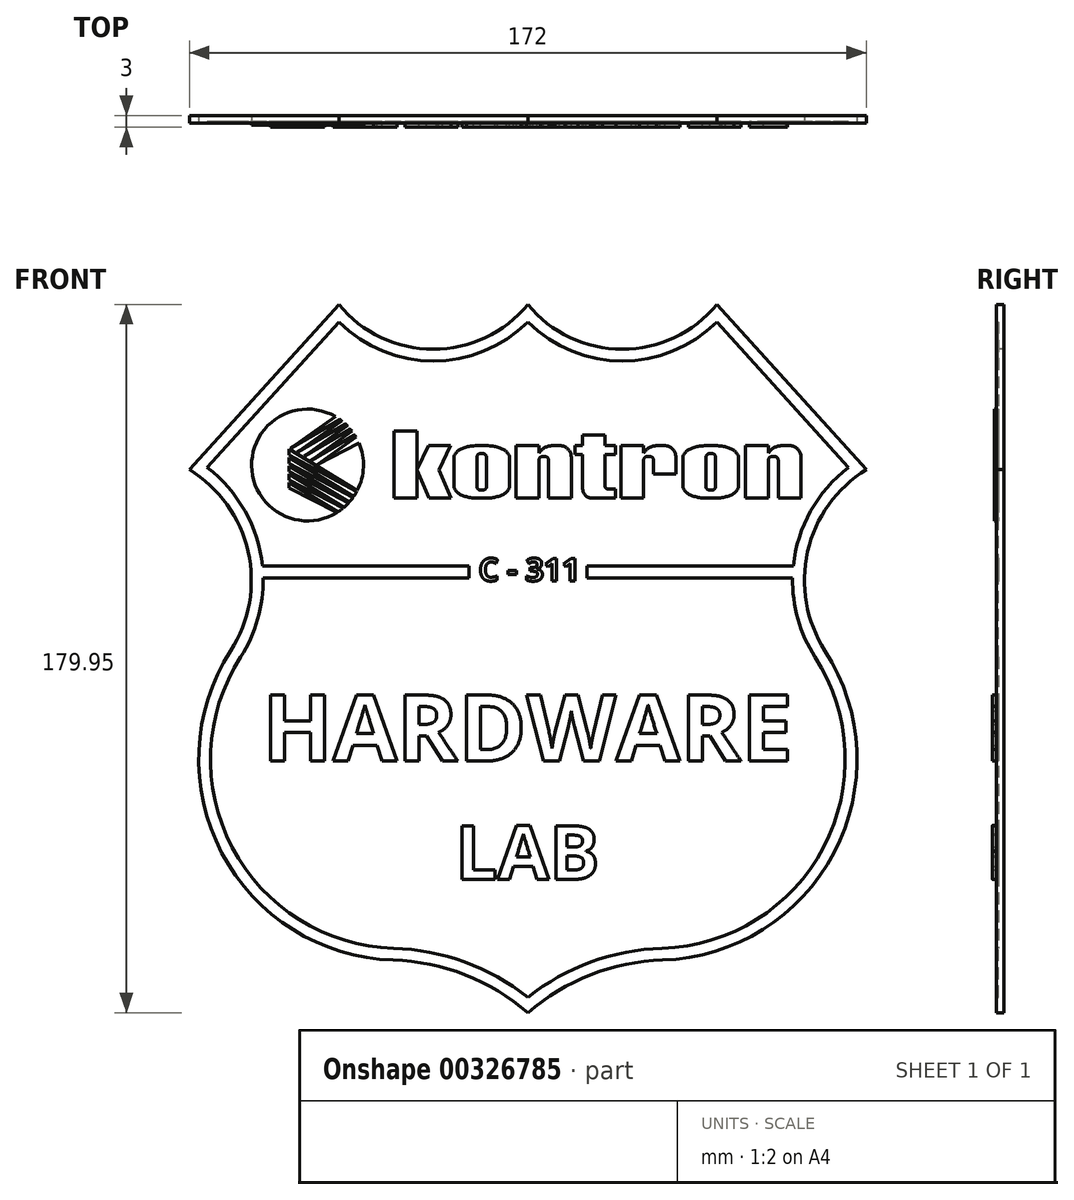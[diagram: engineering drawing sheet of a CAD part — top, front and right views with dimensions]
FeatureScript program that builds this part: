
annotation { "Feature Type Name" : "Feature", "Feature Type Description" : "" }
export const myFeature = defineFeature(function(context is Context, id is Id, definition is map)
    precondition{}
    {
        {
            var Q0;
            Q0=qCreatedBy(makeId("Front.planeOp"),FACE);
            var sketch = newSketch(context, id + "F0", { "sketchPlane" : qUnion([Q0])});
            skLineSegment(sketch, "E0", {"start": v(36.5, 5.8) * mm, "end": v(36.5, 22.8) * mm});
            skLineSegment(sketch, "E1", {"start": v(36.5, 22.8) * mm, "end": v(42.3, 22.8) * mm});
            skLineSegment(sketch, "E2", {"start": v(42.3, 22.8) * mm, "end": v(42.3, 13.1) * mm});
            skLineSegment(sketch, "E3", {"start": v(42.3, 13.1) * mm, "end": v(45.23, 19.1) * mm});
            skLineSegment(sketch, "E4", {"start": v(45.23, 19.1) * mm, "end": v(50.83, 19.1) * mm});
            skLineSegment(sketch, "E5", {"start": v(50.83, 19.1) * mm, "end": v(47.9, 12.9) * mm});
            skLineSegment(sketch, "E6", {"start": v(47.9, 12.9) * mm, "end": v(50.91, 5.8) * mm});
            skLineSegment(sketch, "E7", {"start": v(50.91, 5.8) * mm, "end": v(45.31, 5.8) * mm});
            skLineSegment(sketch, "E8", {"start": v(45.31, 5.8) * mm, "end": v(42.3, 12.9) * mm});
            skLineSegment(sketch, "E9", {"start": v(42.3, 5.8) * mm, "end": v(36.5, 5.8) * mm});
            skLineSegment(sketch, "E10", {"start": v(67.5, 19.1) * mm, "end": v(73.3, 19.1) * mm});
            skLineSegment(sketch, "E11", {"start": v(73.3, 15.4) * mm, "end": v(73.3, 5.8) * mm});
            skLineSegment(sketch, "E12", {"start": v(73.3, 5.8) * mm, "end": v(67.5, 5.8) * mm});
            skLineSegment(sketch, "E13", {"start": v(67.5, 5.8) * mm, "end": v(67.5, 19.1) * mm});
            skLineSegment(sketch, "E14", {"start": v(82.4, 16.8) * mm, "end": v(82.4, 19.1) * mm});
            skLineSegment(sketch, "E15", {"start": v(82.4, 19.1) * mm, "end": v(84.4, 19.1) * mm});
            skLineSegment(sketch, "E16", {"start": v(84.4, 19.1) * mm, "end": v(84.4, 21.8) * mm});
            skLineSegment(sketch, "E17", {"start": v(84.4, 21.8) * mm, "end": v(90.1, 21.8) * mm});
            skLineSegment(sketch, "E18", {"start": v(90.1, 21.8) * mm, "end": v(90.1, 19.1) * mm});
            skLineSegment(sketch, "E19", {"start": v(90.8, 8.1) * mm, "end": v(92.68, 8.1) * mm});
            skLineSegment(sketch, "E20", {"start": v(92.68, 8.1) * mm, "end": v(92.68, 5.8) * mm});
            skLineSegment(sketch, "E21", {"start": v(92.68, 5.8) * mm, "end": v(86.7, 5.8) * mm});
            skLineSegment(sketch, "E22", {"start": v(84.4, 8.1) * mm, "end": v(84.4, 16.8) * mm});
            skLineSegment(sketch, "E23", {"start": v(84.4, 16.8) * mm, "end": v(82.4, 16.8) * mm});
            skLineSegment(sketch, "E24", {"start": v(94.18, 19.1) * mm, "end": v(94.18, 5.8) * mm});
            skLineSegment(sketch, "E25", {"start": v(94.18, 5.8) * mm, "end": v(99.88, 5.8) * mm});
            skLineSegment(sketch, "E26", {"start": v(99.88, 5.8) * mm, "end": v(99.88, 15.4) * mm});
            skLineSegment(sketch, "E27", {"start": v(102.38, 15.4) * mm, "end": v(102.38, 11.9) * mm});
            skLineSegment(sketch, "E28", {"start": v(102.38, 11.9) * mm, "end": v(108.08, 11.9) * mm});
            skLineSegment(sketch, "E29", {"start": v(108.08, 11.9) * mm, "end": v(108.08, 16.2) * mm});
            skLineSegment(sketch, "E30", {"start": v(99.88, 17.2) * mm, "end": v(99.88, 19.1) * mm});
            skLineSegment(sketch, "E31", {"start": v(99.88, 19.1) * mm, "end": v(94.18, 19.1) * mm});
            skLineSegment(sketch, "E32", {"start": v(51.7, 16.1) * mm, "end": v(51.7, 8.8) * mm});
            skLineSegment(sketch, "E33", {"start": v(57.5, 8.8) * mm, "end": v(57.5, 16.1) * mm});
            skLineSegment(sketch, "E34", {"start": v(60, 16.1) * mm, "end": v(60, 8.8) * mm});
            skLineSegment(sketch, "E35", {"start": v(65.8, 8.8) * mm, "end": v(65.8, 16.1) * mm});
            skLineSegment(sketch, "E36", {"start": v(60, 19.1) * mm, "end": v(57.5, 19.1) * mm});
            skLineSegment(sketch, "E37", {"start": v(57.5, 5.8) * mm, "end": v(60, 5.8) * mm});
            skLineSegment(sketch, "E38", {"start": v(115.68, 16.1) * mm, "end": v(115.68, 8.8) * mm});
            skLineSegment(sketch, "E39", {"start": v(118.18, 8.8) * mm, "end": v(118.18, 16.1) * mm});
            skLineSegment(sketch, "E40", {"start": v(123.98, 16.1) * mm, "end": v(123.98, 8.8) * mm});
            skLineSegment(sketch, "E41", {"start": v(109.88, 8.8) * mm, "end": v(109.88, 16.1) * mm});
            skLineSegment(sketch, "E42", {"start": v(125.78, 19.1) * mm, "end": v(125.78, 5.8) * mm});
            skLineSegment(sketch, "E43", {"start": v(125.78, 5.8) * mm, "end": v(131.58, 5.8) * mm});
            skLineSegment(sketch, "E44", {"start": v(131.58, 5.8) * mm, "end": v(131.58, 15.4) * mm});
            skLineSegment(sketch, "E45", {"start": v(134.08, 15.4) * mm, "end": v(134.08, 5.8) * mm});
            skLineSegment(sketch, "E46", {"start": v(134.08, 5.8) * mm, "end": v(139.88, 5.8) * mm});
            skLineSegment(sketch, "E47", {"start": v(139.88, 5.8) * mm, "end": v(139.88, 16.2) * mm});
            skLineSegment(sketch, "E48", {"start": v(136.98, 19.1) * mm, "end": v(134.98, 19.1) * mm});
            skLineSegment(sketch, "E49", {"start": v(131.58, 17.2) * mm, "end": v(131.58, 19.1) * mm});
            skLineSegment(sketch, "E50", {"start": v(131.58, 19.1) * mm, "end": v(125.78, 19.1) * mm});
            skLineSegment(sketch, "E51", {"start": v(75.7, 15.4) * mm, "end": v(75.7, 5.8) * mm});
            skLineSegment(sketch, "E52", {"start": v(75.7, 5.8) * mm, "end": v(81.5, 5.8) * mm});
            skLineSegment(sketch, "E53", {"start": v(81.5, 5.8) * mm, "end": v(81.5, 16.2) * mm});
            skLineSegment(sketch, "E54", {"start": v(42.3, 5.8) * mm, "end": v(42.3, 12.9) * mm});
            skEllipticalArc(sketch, "E55", {});
            skEllipticalArc(sketch, "E56", {});
            skEllipticalArc(sketch, "E57.trimOffspring", {});
            skEllipticalArc(sketch, "E58.trimOffspring", {});
            skLineSegment(sketch, "E59", {"start": v(74.3, 16.4) * mm, "end": v(74.7, 16.4) * mm});
            skArc(sketch, "E60", {"start": v(74.3, 16.4) * mm, "mid": v(73.6, 16.1) * mm, "end": v(73.3, 15.4) * mm});
            skArc(sketch, "E61", {"start": v(75.7, 15.4) * mm, "mid": v(75.4, 16.1) * mm, "end": v(74.7, 16.4) * mm});
            skArc(sketch, "E62", {"start": v(81.5, 16.2) * mm, "mid": v(80.65, 18.25) * mm, "end": v(78.6, 19.1) * mm});
            skLineSegment(sketch, "E63", {"start": v(76.7, 19.1) * mm, "end": v(78.6, 19.1) * mm});
            skLineSegment(sketch, "E64", {"start": v(73.3, 19.1) * mm, "end": v(73.3, 17.2) * mm});
            skArc(sketch, "E65", {"start": v(76.7, 19.1) * mm, "mid": v(74.76, 18.6) * mm, "end": v(73.3, 17.2) * mm});
            skArc(sketch, "E66", {"start": v(84.4, 8.1) * mm, "mid": v(85.07, 6.47) * mm, "end": v(86.7, 5.8) * mm});
            skLineSegment(sketch, "E67", {"start": v(90.1, 19.1) * mm, "end": v(92.68, 19.1) * mm});
            skLineSegment(sketch, "E68", {"start": v(92.68, 19.1) * mm, "end": v(92.68, 16.8) * mm});
            skLineSegment(sketch, "E69", {"start": v(92.68, 16.8) * mm, "end": v(90.1, 16.8) * mm});
            skLineSegment(sketch, "E70", {"start": v(90.1, 16.8) * mm, "end": v(90.1, 8.8) * mm});
            skArc(sketch, "E71", {"start": v(90.1, 8.8) * mm, "mid": v(90.3, 8.3) * mm, "end": v(90.8, 8.1) * mm});
            skLineSegment(sketch, "E72", {"start": v(100.88, 16.4) * mm, "end": v(101.38, 16.4) * mm});
            skLineSegment(sketch, "E73", {"start": v(103.28, 19.1) * mm, "end": v(105.18, 19.1) * mm});
            skArc(sketch, "E74", {"start": v(100.88, 16.4) * mm, "mid": v(100.17, 16.1) * mm, "end": v(99.88, 15.4) * mm});
            skArc(sketch, "E75", {"start": v(102.38, 15.4) * mm, "mid": v(102.08, 16.1) * mm, "end": v(101.38, 16.4) * mm});
            skArc(sketch, "E76", {"start": v(103.28, 19.1) * mm, "mid": v(101.33, 18.6) * mm, "end": v(99.88, 17.2) * mm});
            skArc(sketch, "E77", {"start": v(108.08, 16.2) * mm, "mid": v(107.23, 18.25) * mm, "end": v(105.18, 19.1) * mm});
            skLineSegment(sketch, "E78", {"start": v(115.68, 19.1) * mm, "end": v(118.18, 19.1) * mm});
            skLineSegment(sketch, "E79", {"start": v(116.68, 17.1) * mm, "end": v(117.18, 17.1) * mm});
            skLineSegment(sketch, "E80", {"start": v(117.18, 7.8) * mm, "end": v(116.68, 7.8) * mm});
            skLineSegment(sketch, "E81", {"start": v(115.68, 5.8) * mm, "end": v(118.18, 5.8) * mm});
            skArc(sketch, "E82", {"start": v(116.68, 17.1) * mm, "mid": v(115.97, 16.8) * mm, "end": v(115.68, 16.1) * mm});
            skArc(sketch, "E83", {"start": v(118.18, 16.1) * mm, "mid": v(117.88, 16.8) * mm, "end": v(117.18, 17.1) * mm});
            skArc(sketch, "E84", {"start": v(115.68, 8.8) * mm, "mid": v(115.97, 8.1) * mm, "end": v(116.68, 7.8) * mm});
            skArc(sketch, "E85", {"start": v(117.18, 7.8) * mm, "mid": v(117.88, 8.1) * mm, "end": v(118.18, 8.8) * mm});
            skEllipticalArc(sketch, "E86", {});
            skEllipticalArc(sketch, "E87", {});
            skEllipticalArc(sketch, "E88.trimOffspring", {});
            skEllipticalArc(sketch, "E89.trimOffspring", {});
            skLineSegment(sketch, "E90", {"start": v(132.58, 16.4) * mm, "end": v(133.08, 16.4) * mm});
            skArc(sketch, "E91", {"start": v(132.58, 16.4) * mm, "mid": v(131.87, 16.1) * mm, "end": v(131.58, 15.4) * mm});
            skArc(sketch, "E92", {"start": v(134.08, 15.4) * mm, "mid": v(133.78, 16.1) * mm, "end": v(133.08, 16.4) * mm});
            skArc(sketch, "E93", {"start": v(139.88, 16.2) * mm, "mid": v(139.03, 18.25) * mm, "end": v(136.98, 19.1) * mm});
            skArc(sketch, "E94", {"start": v(134.98, 19.1) * mm, "mid": v(133.03, 18.6) * mm, "end": v(131.58, 17.2) * mm});
            skArc(sketch, "E95", {"start": v(27.13, 7.7) * mm, "mid": v(28.7, 13.68) * mm, "end": v(27.57, 19.75) * mm});
            skLineSegment(sketch, "E96", {"start": v(27.13, 7.7) * mm, "end": v(9.8, 18.2) * mm});
            skLineSegment(sketch, "E97", {"start": v(9.8, 18.2) * mm, "end": v(9.8, 16.7) * mm});
            skLineSegment(sketch, "E98", {"start": v(9.8, 16.7) * mm, "end": v(26.99, 7.44) * mm});
            skLineSegment(sketch, "E99", {"start": v(9.8, 16.1) * mm, "end": v(9.8, 14.6) * mm});
            skLineSegment(sketch, "E100", {"start": v(9.8, 14.6) * mm, "end": v(26.03, 5.92) * mm});
            skLineSegment(sketch, "E101", {"start": v(26.2, 6.16) * mm, "end": v(9.8, 16.1) * mm});
            skLineSegment(sketch, "E102", {"start": v(9.8, 14) * mm, "end": v(9.8, 12.5) * mm});
            skLineSegment(sketch, "E103", {"start": v(9.8, 12.5) * mm, "end": v(24.89, 4.52) * mm});
            skLineSegment(sketch, "E104", {"start": v(25.1, 4.74) * mm, "end": v(9.8, 14) * mm});
            skLineSegment(sketch, "E105", {"start": v(9.8, 11.9) * mm, "end": v(9.8, 10.4) * mm});
            skLineSegment(sketch, "E106", {"start": v(9.8, 10.4) * mm, "end": v(23.54, 3.25) * mm});
            skLineSegment(sketch, "E107", {"start": v(23.77, 3.44) * mm, "end": v(9.8, 11.9) * mm});
            skLineSegment(sketch, "E108", {"start": v(9.8, 9.8) * mm, "end": v(9.8, 8.3) * mm});
            skLineSegment(sketch, "E109", {"start": v(9.8, 8.3) * mm, "end": v(21.96, 2.12) * mm});
            skLineSegment(sketch, "E110", {"start": v(22.22, 2.28) * mm, "end": v(9.8, 9.8) * mm});
            skArc(sketch, "E111.trimOffspring", {"start": v(26.2, 6.16) * mm, "mid": v(26.61, 6.8) * mm, "end": v(26.99, 7.44) * mm});
            skArc(sketch, "E112.trimOffspring", {"start": v(25.1, 4.74) * mm, "mid": v(25.58, 5.32) * mm, "end": v(26.03, 5.92) * mm});
            skArc(sketch, "E113.trimOffspring", {"start": v(23.77, 3.44) * mm, "mid": v(24.34, 3.96) * mm, "end": v(24.89, 4.52) * mm});
            skArc(sketch, "E114.trimOffspring", {"start": v(22.22, 2.28) * mm, "mid": v(22.9, 2.74) * mm, "end": v(23.54, 3.25) * mm});
            skLineSegment(sketch, "E115", {"start": v(21.57, 26.52) * mm, "end": v(10.3, 18.48) * mm});
            skLineSegment(sketch, "E116", {"start": v(10.3, 18.48) * mm, "end": v(22.7, 25.79) * mm});
            skLineSegment(sketch, "E117", {"start": v(23.19, 25.43) * mm, "end": v(12, 17.45) * mm});
            skLineSegment(sketch, "E118", {"start": v(12, 17.45) * mm, "end": v(24.16, 24.6) * mm});
            skLineSegment(sketch, "E119", {"start": v(24.6, 24.2) * mm, "end": v(13.7, 16.42) * mm});
            skLineSegment(sketch, "E120", {"start": v(25.8, 22.8) * mm, "end": v(15.4, 15.4) * mm});
            skLineSegment(sketch, "E121", {"start": v(15.4, 15.4) * mm, "end": v(26.5, 21.8) * mm});
            skLineSegment(sketch, "E122", {"start": v(26.8, 21.29) * mm, "end": v(17.1, 14.36) * mm});
            skLineSegment(sketch, "E123", {"start": v(17.1, 14.36) * mm, "end": v(27.57, 19.75) * mm});
            skArc(sketch, "E124.trimOffspring", {"start": v(21.57, 26.52) * mm, "mid": v(0.3, 13.97) * mm, "end": v(21.96, 2.12) * mm});
            skArc(sketch, "E125.trimOffspring", {"start": v(23.19, 25.43) * mm, "mid": v(22.95, 25.61) * mm, "end": v(22.7, 25.79) * mm});
            skArc(sketch, "E126.trimOffspring", {"start": v(24.6, 24.2) * mm, "mid": v(24.38, 24.4) * mm, "end": v(24.16, 24.6) * mm});
            skArc(sketch, "E127.trimOffspring", {"start": v(25.8, 22.8) * mm, "mid": v(25.6, 23.04) * mm, "end": v(25.42, 23.28) * mm});
            skArc(sketch, "E128.trimOffspring", {"start": v(26.8, 21.29) * mm, "mid": v(26.65, 21.54) * mm, "end": v(26.5, 21.8) * mm});
            skLineSegment(sketch, "E129", {"start": v(25.42, 23.28) * mm, "end": v(13.7, 16.42) * mm});
            skLineSegment(sketch, "E130", {"start": v(58.5, 17.1) * mm, "end": v(59, 17.1) * mm});
            skLineSegment(sketch, "E131", {"start": v(59, 7.8) * mm, "end": v(58.5, 7.8) * mm});
            skArc(sketch, "E132", {"start": v(58.5, 17.1) * mm, "mid": v(57.8, 16.8) * mm, "end": v(57.5, 16.1) * mm});
            skArc(sketch, "E133", {"start": v(60, 16.1) * mm, "mid": v(59.7, 16.8) * mm, "end": v(59, 17.1) * mm});
            skArc(sketch, "E134", {"start": v(59, 7.8) * mm, "mid": v(59.7, 8.1) * mm, "end": v(60, 8.8) * mm});
            skArc(sketch, "E135", {"start": v(57.5, 8.8) * mm, "mid": v(57.8, 8.1) * mm, "end": v(58.5, 7.8) * mm});
            skLineSegment(sketch, "E136", {"start": v(118.46, 55) * mm, "end": v(156.46, 13) * mm});
            skLineSegment(sketch, "E137", {"start": v(22.46, 55) * mm, "end": v(-15.54, 13) * mm});
            skArc(sketch, "E138", {"start": v(22.46, 55) * mm, "mid": v(46.46, 43.62) * mm, "end": v(70.46, 55) * mm});
            skArc(sketch, "E139", {"start": v(70.46, 55) * mm, "mid": v(94.46, 43.62) * mm, "end": v(118.46, 55) * mm});
            skArc(sketch, "E140", {"start": v(-5.04, -33) * mm, "mid": v(-0.61, -7.8) * mm, "end": v(-15.54, 13) * mm});
            skArc(sketch, "E141", {"start": v(-5.04, -33) * mm, "mid": v(-7.3, -84.32) * mm, "end": v(36.23, -111.58) * mm});
            skArc(sketch, "E142", {"start": v(70.46, -124.95) * mm, "mid": v(54.5, -115.32) * mm, "end": v(36.23, -111.58) * mm});
            skArc(sketch, "E143", {"start": v(104.7, -111.58) * mm, "mid": v(86.43, -115.32) * mm, "end": v(70.46, -124.95) * mm});
            skArc(sketch, "E144", {"start": v(104.7, -111.58) * mm, "mid": v(148.23, -84.32) * mm, "end": v(145.96, -33) * mm});
            skArc(sketch, "E145", {"start": v(156.46, 13) * mm, "mid": v(141.54, -7.8) * mm, "end": v(145.96, -33) * mm});
            const initialGuessF0  = {"E55": [0.06, 0.0161, 0, 1, 0.003, 0.0058, 4.71238898038469, 6.283185307179586], "E56": [0.06, 0.0088, 0, -1, 0.003, 0.0058, 6.283185307179586, 1.5707963267948966], "E57.trimOffspring": [0.0575, 0.0161, -1, 0, 0.0058, 0.003, 4.71238898038469, 0], "E58.trimOffspring": [0.0575, 0.0088, 0, -1, 0.003, 0.0058, 4.71238898038469, 6.283185307179586], "E86": [0.11567681705125998, 0.0088, 0, -1, 0.003, 0.0058, 4.71238898038469, 6.283185307179586], "E87": [0.11567681705126001, 0.0161, -1, 0, 0.0058, 0.003, 4.71238898038469, 0], "E88.trimOffspring": [0.11817681705126001, 0.0161, 1, 0, 0.0058, 0.003, 0, 1.570796326794896], "E89.trimOffspring": [0.11817681705125999, 0.0088, 1, 0, 0.0058, 0.003, 4.71238898038469, 0]};
            skSetInitialGuess(sketch, initialGuessF0);
            skSolve(sketch);
        }
        {
            var Q0;
            Q0=makeQuery(id+"F0.imprint","IMPRINT",FACE,{"disambiguationData":[TD([[makeQuery(id+"F0.imprint","IMPRINT",EDGE,{"derivedFrom":sQuery(id+"F0.wireOp",EDGE,"E0")}),1.0]])]});
            var Q1;
            Q1=makeQuery(id+"F0.imprint","IMPRINT",FACE,{"disambiguationData":[TD([[makeQuery(id+"F0.imprint","IMPRINT",EDGE,{"derivedFrom":sQuery(id+"F0.wireOp",EDGE,"E95")}),1.0]])]});
            var Q2;
            Q2=makeQuery(id+"F0.imprint","IMPRINT",FACE,{"disambiguationData":[TD([[makeQuery(id+"F0.imprint","IMPRINT",EDGE,{"derivedFrom":sQuery(id+"F0.wireOp",EDGE,"E0")}),-1.0]])]});
            var Q3;
            Q3=makeQuery(id+"F0.imprint","IMPRINT",FACE,{"disambiguationData":[TD([[makeQuery(id+"F0.imprint","IMPRINT",EDGE,{"derivedFrom":sQuery(id+"F0.wireOp",EDGE,"E32")}),1.0]])]});
            var Q4;
            Q4=makeQuery(id+"F0.imprint","IMPRINT",FACE,{"disambiguationData":[TD([[makeQuery(id+"F0.imprint","IMPRINT",EDGE,{"derivedFrom":sQuery(id+"F0.wireOp",EDGE,"E3")}),-1.0]])]});
            var Q5;
            Q5=makeQuery(id+"F0.imprint","IMPRINT",FACE,{"disambiguationData":[TD([[makeQuery(id+"F0.imprint","IMPRINT",EDGE,{"derivedFrom":sQuery(id+"F0.wireOp",EDGE,"E10")}),-1.0]])]});
            var Q6;
            Q6=makeQuery(id+"F0.imprint","IMPRINT",FACE,{"disambiguationData":[TD([[makeQuery(id+"F0.imprint","IMPRINT",EDGE,{"derivedFrom":sQuery(id+"F0.wireOp",EDGE,"E14")}),-1.0]])]});
            var Q7;
            Q7=makeQuery(id+"F0.imprint","IMPRINT",FACE,{"disambiguationData":[TD([[makeQuery(id+"F0.imprint","IMPRINT",EDGE,{"derivedFrom":sQuery(id+"F0.wireOp",EDGE,"E33")}),-1.0]])]});
            var Q8;
            Q8=makeQuery(id+"F0.imprint","IMPRINT",FACE,{"disambiguationData":[TD([[makeQuery(id+"F0.imprint","IMPRINT",EDGE,{"derivedFrom":sQuery(id+"F0.wireOp",EDGE,"E24")}),1.0]])]});
            var Q9;
            Q9=makeQuery(id+"F0.imprint","IMPRINT",FACE,{"disambiguationData":[TD([[makeQuery(id+"F0.imprint","IMPRINT",EDGE,{"derivedFrom":sQuery(id+"F0.wireOp",EDGE,"E38")}),-1.0]])]});
            var Q10;
            Q10=makeQuery(id+"F0.imprint","IMPRINT",FACE,{"disambiguationData":[TD([[makeQuery(id+"F0.imprint","IMPRINT",EDGE,{"derivedFrom":sQuery(id+"F0.wireOp",EDGE,"E38")}),1.0]])]});
            var Q11;
            Q11=makeQuery(id+"F0.imprint","IMPRINT",FACE,{"disambiguationData":[TD([[makeQuery(id+"F0.imprint","IMPRINT",EDGE,{"derivedFrom":sQuery(id+"F0.wireOp",EDGE,"E42")}),1.0]])]});
            extrude(context, id + "F1", {"entities" : qUnion([Q0, Q1, Q2, Q3, Q4, Q5, Q6, Q7, Q8, Q9, Q10, Q11]), "oppositeDirection" : true, "depth" : 1.5 * mm});
        }
        {
            var Q0;
            Q0=makeQuery(id+"F0.imprint","IMPRINT",FACE,{"disambiguationData":[TD([[makeQuery(id+"F0.imprint","IMPRINT",EDGE,{"derivedFrom":sQuery(id+"F0.wireOp",EDGE,"E0")}),-1.0]])]});
            var Q1;
            Q1=makeQuery(id+"F0.imprint","IMPRINT",FACE,{"disambiguationData":[TD([[makeQuery(id+"F0.imprint","IMPRINT",EDGE,{"derivedFrom":sQuery(id+"F0.wireOp",EDGE,"E32")}),1.0]])]});
            var Q2;
            Q2=makeQuery(id+"F0.imprint","IMPRINT",FACE,{"disambiguationData":[TD([[makeQuery(id+"F0.imprint","IMPRINT",EDGE,{"derivedFrom":sQuery(id+"F0.wireOp",EDGE,"E10")}),-1.0]])]});
            var Q3;
            Q3=makeQuery(id+"F0.imprint","IMPRINT",FACE,{"disambiguationData":[TD([[makeQuery(id+"F0.imprint","IMPRINT",EDGE,{"derivedFrom":sQuery(id+"F0.wireOp",EDGE,"E14")}),-1.0]])]});
            var Q4;
            Q4=makeQuery(id+"F0.imprint","IMPRINT",FACE,{"disambiguationData":[TD([[makeQuery(id+"F0.imprint","IMPRINT",EDGE,{"derivedFrom":sQuery(id+"F0.wireOp",EDGE,"E24")}),1.0]])]});
            var Q5;
            Q5=makeQuery(id+"F0.imprint","IMPRINT",FACE,{"disambiguationData":[TD([[makeQuery(id+"F0.imprint","IMPRINT",EDGE,{"derivedFrom":sQuery(id+"F0.wireOp",EDGE,"E38")}),-1.0]])]});
            var Q6;
            Q6=makeQuery(id+"F0.imprint","IMPRINT",FACE,{"disambiguationData":[TD([[makeQuery(id+"F0.imprint","IMPRINT",EDGE,{"derivedFrom":sQuery(id+"F0.wireOp",EDGE,"E42")}),1.0]])]});
            extrude(context, id + "F2", {"entities" : qUnion([Q0, Q1, Q2, Q3, Q4, Q5, Q6]), "operationType" : NewBodyOperationType.ADD, "depth" : 0.5 * mm});
        }
        {
            var Q0;
            {var subQ0=sQuery(id+"F0.wireOp",EDGE,"E138");var subQ1=sQuery(id+"F0.wireOp",EDGE,"E137");var subQ2=sQuery(id+"F0.wireOp",EDGE,"E139");var subQ3=sQuery(id+"F0.wireOp",EDGE,"E136");var subQ4=sQuery(id+"F0.wireOp",EDGE,"E145");var subQ5=sQuery(id+"F0.wireOp",EDGE,"E141");var subQ6=sQuery(id+"F0.wireOp",EDGE,"E142");var subQ7=sQuery(id+"F0.wireOp",EDGE,"E140");var subQ8=sQuery(id+"F0.wireOp",EDGE,"E143");var subQ9=sQuery(id+"F0.wireOp",EDGE,"E144");Q0=makeQuery(id+"F2.boolean.opBoolean","SPLIT",FACE,{"disambiguationData":[TD([makeQuery(id+"F1.opExtrude","SWEPT_FACE",FACE,{"disambiguationData":[OSD([subQ3])]})])],"derivedFrom":makeQuery(id+"F1.opExtrude","CAP_FACE",FACE,{"disambiguationData":[OSD([subQ3,subQ1,subQ0,subQ2,subQ7,subQ5,subQ6,subQ8,subQ9,subQ4])],"isStart":true})});}
            var sketch = newSketch(context, id + "F3", { "sketchPlane" : qUnion([Q0])});
            skLineSegment(sketch, "E146.bottom", {"start": v(3.03, -11.46) * mm, "end": v(55.46, -11.46) * mm});
            skLineSegment(sketch, "E146.top", {"start": v(3.21, -14.46) * mm, "end": v(55.46, -14.46) * mm});
            skLineSegment(sketch, "E146.right", {"start": v(55.46, -11.46) * mm, "end": v(55.46, -14.46) * mm});
            skLineSegment(sketch, "E147.bottom", {"start": v(85.46, -11.46) * mm, "end": v(137.9, -11.46) * mm});
            skLineSegment(sketch, "E147.top", {"start": v(85.46, -14.46) * mm, "end": v(137.71, -14.46) * mm});
            skLineSegment(sketch, "E147.left", {"start": v(85.46, -11.46) * mm, "end": v(85.46, -14.46) * mm});
            skLineSegment(sketch, "E148", {"start": v(22.46, 55) * mm, "end": v(-15.54, 13) * mm});
            skArc(sketch, "E149", {"start": v(-5.04, -33) * mm, "mid": v(-0.61, -7.8) * mm, "end": v(-15.54, 13) * mm});
            skArc(sketch, "E150", {"start": v(-5.04, -33) * mm, "mid": v(-7.3, -84.32) * mm, "end": v(36.23, -111.58) * mm});
            skArc(sketch, "E151", {"start": v(70.46, -124.95) * mm, "mid": v(54.5, -115.32) * mm, "end": v(36.23, -111.58) * mm});
            skArc(sketch, "E152", {"start": v(104.7, -111.58) * mm, "mid": v(86.43, -115.32) * mm, "end": v(70.46, -124.95) * mm});
            skArc(sketch, "E153", {"start": v(104.7, -111.58) * mm, "mid": v(148.23, -84.32) * mm, "end": v(145.96, -33) * mm});
            skArc(sketch, "E154", {"start": v(156.46, 13) * mm, "mid": v(141.54, -7.8) * mm, "end": v(145.96, -33) * mm});
            skArc(sketch, "E155", {"start": v(22.46, 55) * mm, "mid": v(46.46, 43.62) * mm, "end": v(70.46, 55) * mm});
            skArc(sketch, "E156", {"start": v(70.46, 55) * mm, "mid": v(94.46, 43.62) * mm, "end": v(118.46, 55) * mm});
            skLineSegment(sketch, "E157", {"start": v(118.46, 55) * mm, "end": v(156.46, 13) * mm});
            skArc(sketch, "E158.0", {"start": v(22.47, 50.53) * mm, "mid": v(46.47, 40.62) * mm, "end": v(70.46, 50.54) * mm});
            skLineSegment(sketch, "E158.1", {"start": v(22.47, 50.53) * mm, "end": v(-11, 13.53) * mm});
            skArc(sketch, "E158.2", {"start": v(70.46, 50.54) * mm, "mid": v(94.46, 40.62) * mm, "end": v(118.46, 50.53) * mm});
            skArc(sketch, "E158.3", {"start": v(-2.52, -34.62) * mm, "mid": v(1.85, -24.97) * mm, "end": v(3.21, -14.46) * mm});
            skArc(sketch, "E158.4", {"start": v(-2.52, -34.62) * mm, "mid": v(-4.65, -82.93) * mm, "end": v(36.33, -108.59) * mm});
            skArc(sketch, "E158.5", {"start": v(70.46, -121.05) * mm, "mid": v(54.4, -112.08) * mm, "end": v(36.33, -108.59) * mm});
            skLineSegment(sketch, "E158.6", {"start": v(118.46, 50.53) * mm, "end": v(151.93, 13.53) * mm});
            skArc(sketch, "E158.7", {"start": v(151.93, 13.53) * mm, "mid": v(142.32, 2.5) * mm, "end": v(137.9, -11.46) * mm});
            skArc(sketch, "E158.8", {"start": v(104.6, -108.59) * mm, "mid": v(145.58, -82.93) * mm, "end": v(143.44, -34.62) * mm});
            skArc(sketch, "E158.9", {"start": v(104.6, -108.59) * mm, "mid": v(86.53, -112.08) * mm, "end": v(70.46, -121.05) * mm});
            skArc(sketch, "E159.trimOffspring", {"start": v(3.03, -11.46) * mm, "mid": v(-1.4, 2.5) * mm, "end": v(-11, 13.53) * mm});
            skArc(sketch, "E160.trimOffspring", {"start": v(137.71, -14.46) * mm, "mid": v(139.08, -24.97) * mm, "end": v(143.44, -34.62) * mm});
            skSolve(sketch);
        }
        {
            var Q0;
            Q0 = qSketchRegion(id + "F3", true);
            extrude(context, id + "F4", {"entities" : qUnion([Q0]), "operationType" : NewBodyOperationType.ADD, "depth" : 0.5 * mm});
        }
        {
            var Q0;
            {var subQ0=sQuery(id+"F0.wireOp",EDGE,"E138");var subQ1=sQuery(id+"F0.wireOp",EDGE,"E137");var subQ2=sQuery(id+"F0.wireOp",EDGE,"E139");var subQ3=sQuery(id+"F0.wireOp",EDGE,"E136");var subQ4=sQuery(id+"F0.wireOp",EDGE,"E145");var subQ5=sQuery(id+"F0.wireOp",EDGE,"E141");var subQ6=sQuery(id+"F0.wireOp",EDGE,"E142");var subQ7=sQuery(id+"F0.wireOp",EDGE,"E140");var subQ8=sQuery(id+"F0.wireOp",EDGE,"E143");var subQ9=sQuery(id+"F0.wireOp",EDGE,"E144");Q0=makeQuery(id+"F2.boolean.opBoolean","SPLIT",FACE,{"disambiguationData":[TD([makeQuery(id+"F1.opExtrude","SWEPT_FACE",FACE,{"disambiguationData":[OSD([subQ3])]})])],"derivedFrom":makeQuery(id+"F1.opExtrude","CAP_FACE",FACE,{"disambiguationData":[OSD([subQ3,subQ1,subQ0,subQ2,subQ7,subQ5,subQ6,subQ8,subQ9,subQ4])],"isStart":true})});}
            var sketch = newSketch(context, id + "F5", { "sketchPlane" : qUnion([Q0])});
            skText(sketch, "E161", { "text": "C - 311", "fontName": "OpenSans-Bold.ttf"});
            const initialGuessF5  = {"E161": [0.05796, -0.01527, 1, 0, 0.0058]};
            skSetInitialGuess(sketch, initialGuessF5);
            skSolve(sketch);
        }
        {
            var Q0;
            Q0 = qSketchRegion(id + "F5", true);
            extrude(context, id + "F6", {"entities" : qUnion([Q0]), "operationType" : NewBodyOperationType.ADD, "depth" : 0.5 * mm});
        }
        {
            var Q0;
            {var subQ0=sQuery(id+"F0.wireOp",EDGE,"E138");var subQ1=sQuery(id+"F0.wireOp",EDGE,"E137");var subQ2=sQuery(id+"F0.wireOp",EDGE,"E139");var subQ3=sQuery(id+"F0.wireOp",EDGE,"E136");var subQ4=sQuery(id+"F0.wireOp",EDGE,"E145");var subQ5=sQuery(id+"F0.wireOp",EDGE,"E141");var subQ6=sQuery(id+"F0.wireOp",EDGE,"E142");var subQ7=sQuery(id+"F0.wireOp",EDGE,"E140");var subQ8=sQuery(id+"F0.wireOp",EDGE,"E143");var subQ9=sQuery(id+"F0.wireOp",EDGE,"E144");Q0=makeQuery(id+"F2.boolean.opBoolean","SPLIT",FACE,{"disambiguationData":[TD([makeQuery(id+"F1.opExtrude","SWEPT_FACE",FACE,{"disambiguationData":[OSD([subQ3])]})])],"derivedFrom":makeQuery(id+"F1.opExtrude","CAP_FACE",FACE,{"disambiguationData":[OSD([subQ3,subQ1,subQ0,subQ2,subQ7,subQ5,subQ6,subQ8,subQ9,subQ4])],"isStart":true})});}
            var sketch = newSketch(context, id + "F7", { "sketchPlane" : qUnion([Q0])});
            skText(sketch, "E162", { "text": "HARDWARE", "fontName": "OpenSans-Bold.ttf"});
            const initialGuessF7  = {"E162": [0.00296, -0.06105, 1, 0, 0.01694]};
            skSetInitialGuess(sketch, initialGuessF7);
            skSolve(sketch);
        }
        {
            var Q0;
            Q0 = qSketchRegion(id + "F7", true);
            extrude(context, id + "F8", {"entities" : qUnion([Q0]), "operationType" : NewBodyOperationType.ADD, "depth" : 1.5 * mm});
        }
        {
            var Q0;
            Q0=makeQuery(id+"F0.imprint","IMPRINT",FACE,{"disambiguationData":[TD([[makeQuery(id+"F0.imprint","IMPRINT",EDGE,{"derivedFrom":sQuery(id+"F0.wireOp",EDGE,"E95")}),1.0]])]});
            extrude(context, id + "F9", {"entities" : qUnion([Q0]), "operationType" : NewBodyOperationType.ADD, "depth" : 1 * mm});
        }
        {
            var Q0;
            {var subQ29=makeQuery(id+"F2.opExtrude","SWEPT_FACE",FACE,{"disambiguationData":[OSD([sQuery(id+"F0.wireOp",EDGE,"E0")])]});var subQ85=sQuery(id+"F0.wireOp",EDGE,"E144");var subQ86=sQuery(id+"F0.wireOp",EDGE,"E143");var subQ87=sQuery(id+"F0.wireOp",EDGE,"E140");var subQ88=sQuery(id+"F0.wireOp",EDGE,"E142");var subQ89=sQuery(id+"F0.wireOp",EDGE,"E141");var subQ90=sQuery(id+"F0.wireOp",EDGE,"E145");var subQ91=sQuery(id+"F0.wireOp",EDGE,"E136");var subQ92=sQuery(id+"F0.wireOp",EDGE,"E139");var subQ93=sQuery(id+"F0.wireOp",EDGE,"E137");var subQ94=sQuery(id+"F0.wireOp",EDGE,"E138");Q0=makeQuery(id+"F8.boolean.opBoolean","SPLIT",FACE,{"disambiguationData":[TD([subQ29])],"derivedFrom":makeQuery(id+"F2.boolean.opBoolean","SPLIT",FACE,{"disambiguationData":[TD([makeQuery(id+"F1.opExtrude","SWEPT_FACE",FACE,{"disambiguationData":[OSD([subQ91])]})])],"derivedFrom":makeQuery(id+"F1.opExtrude","CAP_FACE",FACE,{"disambiguationData":[OSD([subQ91,subQ93,subQ94,subQ92,subQ87,subQ89,subQ88,subQ86,subQ85,subQ90])],"isStart":true})})});}
            var sketch = newSketch(context, id + "F10", { "sketchPlane" : qUnion([Q0])});
            skText(sketch, "E163", { "text": "LAB", "fontName": "OpenSans-Bold.ttf"});
            const initialGuessF10  = {"E163": [0.05203, -0.09105, 1, 0, 0.01368]};
            skSetInitialGuess(sketch, initialGuessF10);
            skSolve(sketch);
        }
        {
            var Q0;
            Q0 = qSketchRegion(id + "F10", true);
            var Q1;
            Q1=makeQuery(id+"F8.opExtrude","CAP_FACE",FACE,{"disambiguationData":[OSD([sQuery(id+"F7.wireOp",EDGE,"E162.sketch_text.stroke-0"),sQuery(id+"F7.wireOp",EDGE,"E162.sketch_text.stroke-1"),sQuery(id+"F7.wireOp",EDGE,"E162.sketch_text.stroke-2"),sQuery(id+"F7.wireOp",EDGE,"E162.sketch_text.stroke-3"),sQuery(id+"F7.wireOp",EDGE,"E162.sketch_text.stroke-4"),sQuery(id+"F7.wireOp",EDGE,"E162.sketch_text.stroke-5"),sQuery(id+"F7.wireOp",EDGE,"E162.sketch_text.stroke-6"),sQuery(id+"F7.wireOp",EDGE,"E162.sketch_text.stroke-7"),sQuery(id+"F7.wireOp",EDGE,"E162.sketch_text.stroke-8"),sQuery(id+"F7.wireOp",EDGE,"E162.sketch_text.stroke-9"),sQuery(id+"F7.wireOp",EDGE,"E162.sketch_text.stroke-10"),sQuery(id+"F7.wireOp",EDGE,"E162.sketch_text.stroke-11")])],"isStart":false});
            extrude(context, id + "F11", {"entities" : qUnion([Q0]), "operationType" : NewBodyOperationType.ADD, "endBound" : BoundingType.UP_TO_SURFACE, "endBoundEntityFace" : qUnion([Q1]), "depth" : 25 * mm});
        }
    });
